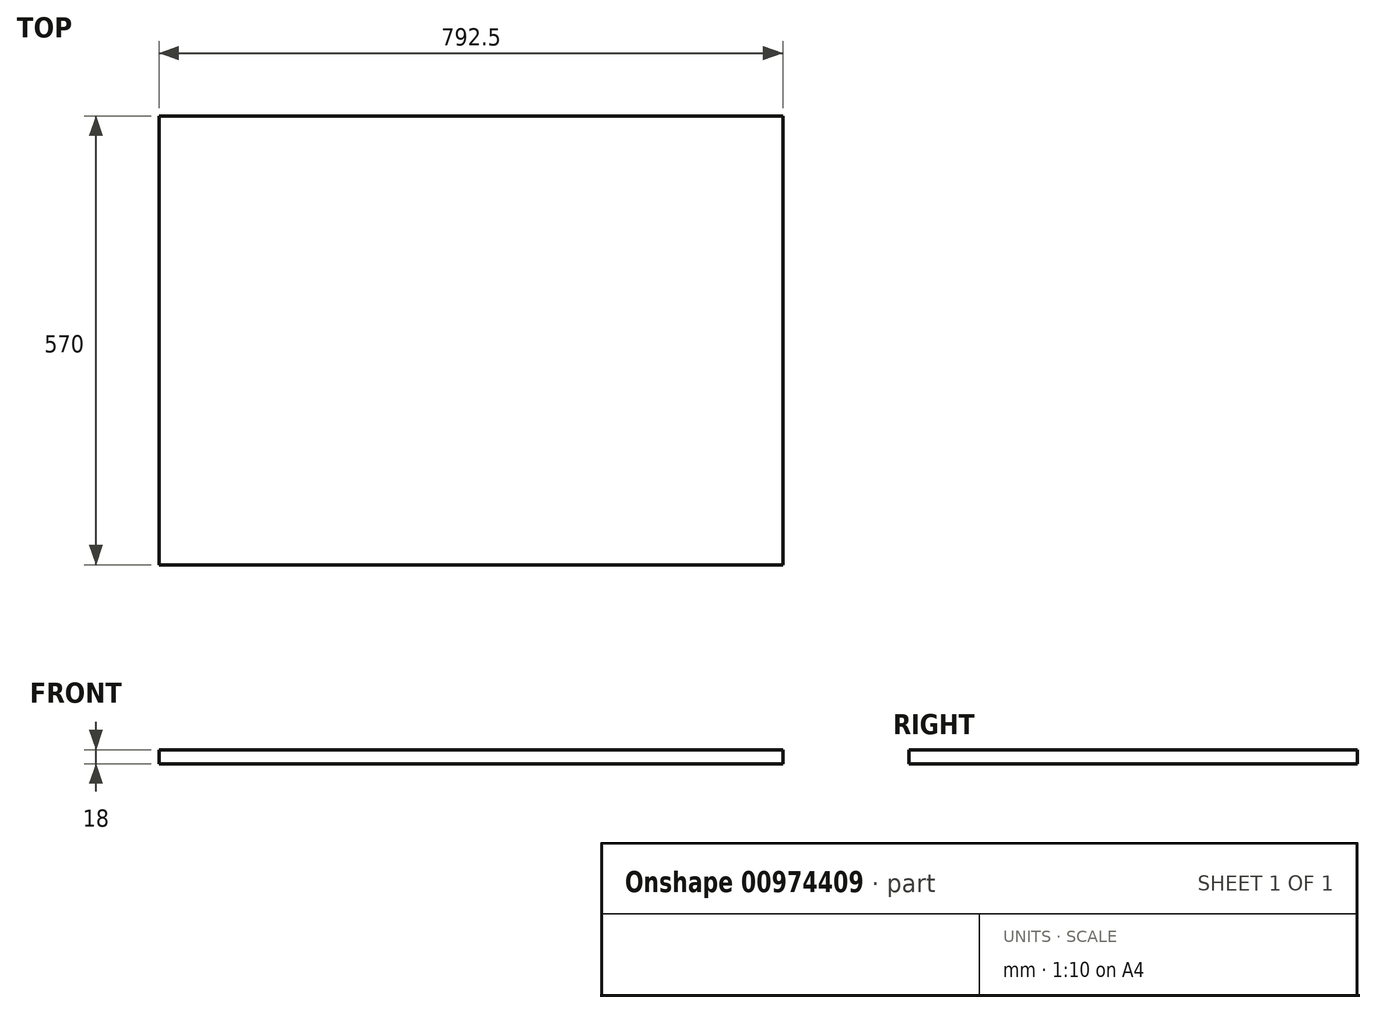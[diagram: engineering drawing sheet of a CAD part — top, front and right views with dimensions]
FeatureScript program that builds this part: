
annotation { "Feature Type Name" : "Feature", "Feature Type Description" : "" }
export const myFeature = defineFeature(function(context is Context, id is Id, definition is map)
    precondition{}
    {
        {
            var Q0;
            Q0=qCreatedBy(makeId("Top.planeOp"),FACE);
            var sketch = newSketch(context, id + "F0", { "sketchPlane" : qUnion([Q0])});
            skLineSegment(sketch, "E0.bottom", {"start": v(396.25, 285) * mm, "end": v(-396.25, 285) * mm});
            skLineSegment(sketch, "E0.top", {"start": v(396.25, -285) * mm, "end": v(-396.25, -285) * mm});
            skLineSegment(sketch, "E0.left", {"start": v(396.25, 285) * mm, "end": v(396.25, -285) * mm});
            skLineSegment(sketch, "E0.right", {"start": v(-396.25, 285) * mm, "end": v(-396.25, -285) * mm});
            skPoint(sketch, "E0.middle", {"position": v(0, 0) * mm});
            skSolve(sketch);
        }
        {
            var Q0;
            Q0=makeQuery(id+"F0.imprint","IMPRINT",FACE,{"disambiguationData":[TD([[makeQuery(id+"F0.imprint","IMPRINT",EDGE,{"derivedFrom":sQuery(id+"F0.wireOp",EDGE,"E0.bottom")}),1.0]])]});
            extrude(context, id + "F1", {"entities" : qUnion([Q0]), "depth" : 18 * mm, "offsetDistance" : 25 * mm});
        }
    });
